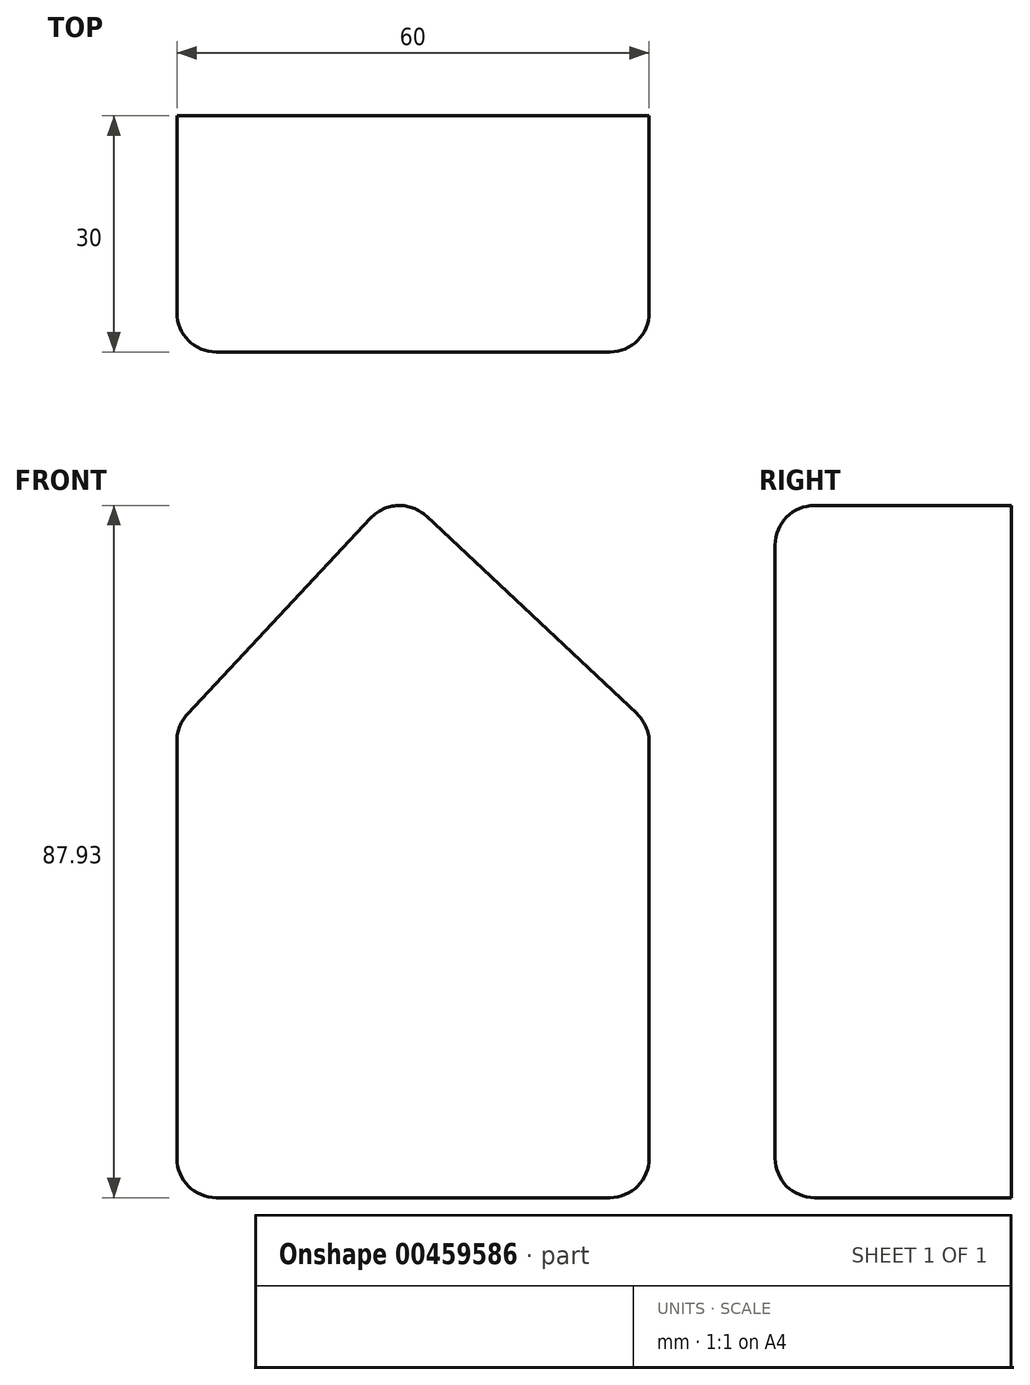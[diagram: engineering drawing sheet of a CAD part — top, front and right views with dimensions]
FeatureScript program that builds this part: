
annotation { "Feature Type Name" : "Feature", "Feature Type Description" : "" }
export const myFeature = defineFeature(function(context is Context, id is Id, definition is map)
    precondition{}
    {
        {
            var Q0;
            Q0=qCreatedBy(makeId("Front.planeOp"),FACE);
            var sketch = newSketch(context, id + "F0", { "sketchPlane" : qUnion([Q0])});
            skLineSegment(sketch, "E0", {"start": v(-28.03, 30) * mm, "end": v(-28.03, -30) * mm});
            skLineSegment(sketch, "E1", {"start": v(-28.03, -30) * mm, "end": v(31.97, -30) * mm});
            skLineSegment(sketch, "E2", {"start": v(31.97, -30) * mm, "end": v(31.97, 30) * mm});
            skLineSegment(sketch, "E3", {"start": v(31.97, 30) * mm, "end": v(0, 60) * mm});
            skLineSegment(sketch, "E4", {"start": v(0, 60) * mm, "end": v(-28.03, 30) * mm});
            skSolve(sketch);
        }
        {
            var Q0;
            Q0 = qSketchRegion(id + "F0", true);
            extrude(context, id + "F1", {"entities" : qUnion([Q0]), "depth" : 30 * mm});
        }
        {
            var Q0;
            Q0=makeQuery(id+"F1.opExtrude","CAP_EDGE",EDGE,{"disambiguationData":[OSD([sQuery(id+"F0.wireOp",EDGE,"E4")])],"isStart":false});
            var Q1;
            Q1=makeQuery(id+"F1.opExtrude","CAP_EDGE",EDGE,{"disambiguationData":[OSD([sQuery(id+"F0.wireOp",EDGE,"E3")])],"isStart":false});
            var Q2;
            Q2=makeQuery(id+"F1.opExtrude","CAP_EDGE",EDGE,{"disambiguationData":[OSD([sQuery(id+"F0.wireOp",EDGE,"E0")])],"isStart":false});
            var Q3;
            Q3=makeQuery(id+"F1.opExtrude","SWEPT_EDGE",EDGE,{"disambiguationData":[OSD([sQuery(id+"F0.wireOp",EDGE,"E0"),sQuery(id+"F0.wireOp",EDGE,"E4")])]});
            var Q4;
            Q4=makeQuery(id+"F1.opExtrude","SWEPT_EDGE",EDGE,{"disambiguationData":[OSD([sQuery(id+"F0.wireOp",EDGE,"E3"),sQuery(id+"F0.wireOp",EDGE,"E4")])]});
            var Q5;
            Q5=makeQuery(id+"F1.opExtrude","CAP_EDGE",EDGE,{"disambiguationData":[OSD([sQuery(id+"F0.wireOp",EDGE,"E2")])],"isStart":false});
            var Q6;
            Q6=makeQuery(id+"F1.opExtrude","CAP_EDGE",EDGE,{"disambiguationData":[OSD([sQuery(id+"F0.wireOp",EDGE,"E1")])],"isStart":false});
            var Q7;
            Q7=makeQuery(id+"F1.opExtrude","SWEPT_EDGE",EDGE,{"disambiguationData":[OSD([sQuery(id+"F0.wireOp",EDGE,"E0"),sQuery(id+"F0.wireOp",EDGE,"E1")])]});
            var Q8;
            Q8=makeQuery(id+"F1.opExtrude","SWEPT_EDGE",EDGE,{"disambiguationData":[OSD([sQuery(id+"F0.wireOp",EDGE,"E1"),sQuery(id+"F0.wireOp",EDGE,"E2")])]});
            var Q9;
            Q9=makeQuery(id+"F1.opExtrude","SWEPT_EDGE",EDGE,{"disambiguationData":[OSD([sQuery(id+"F0.wireOp",EDGE,"E2"),sQuery(id+"F0.wireOp",EDGE,"E3")])]});
            fillet(context, id + "F2", {"entities" : qUnion([Q0, Q1, Q2, Q3, Q4, Q5, Q6, Q7, Q8, Q9]), "radius" : 5 * mm, "tangentPropagation" : true, "allowEdgeOverflow" : false});
        }
    });
